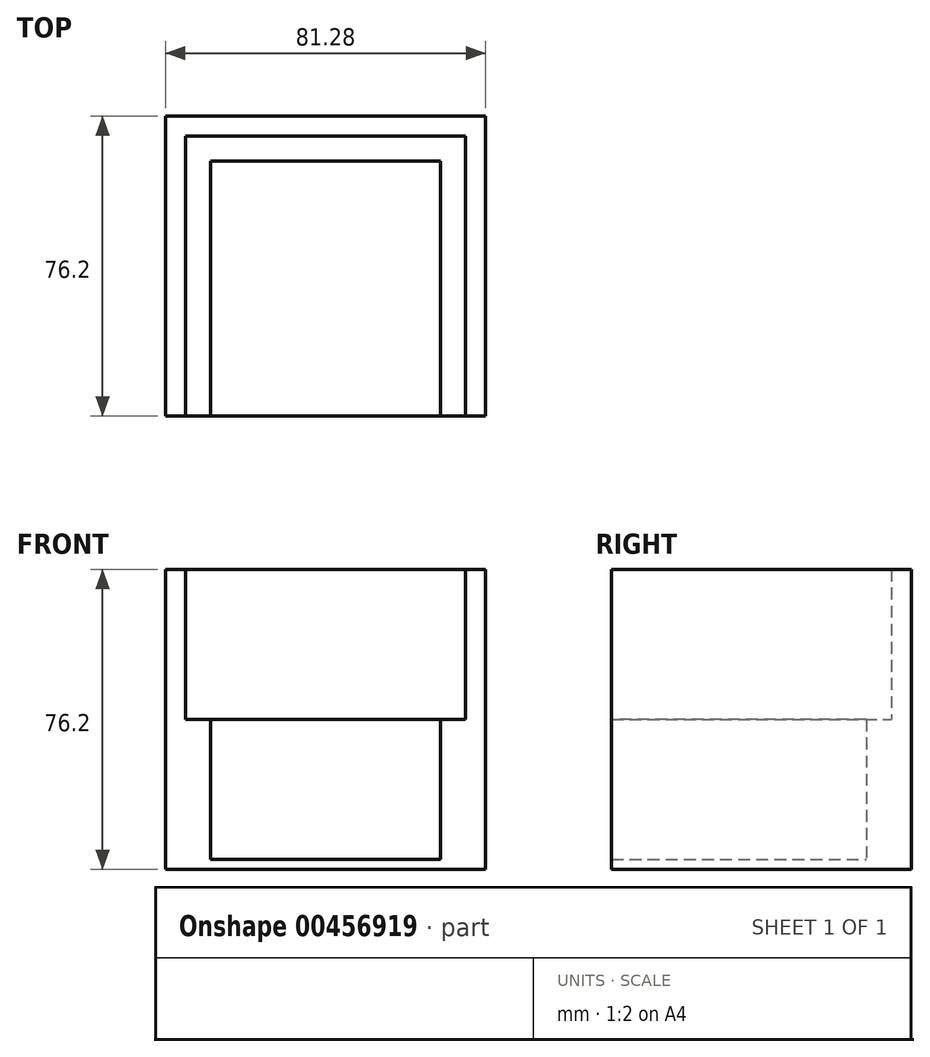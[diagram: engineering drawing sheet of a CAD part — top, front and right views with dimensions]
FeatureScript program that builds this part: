
annotation { "Feature Type Name" : "Feature", "Feature Type Description" : "" }
export const myFeature = defineFeature(function(context is Context, id is Id, definition is map)
    precondition{}
    {
        {
            var Q0;
            Q0=qCreatedBy(makeId("Top.planeOp"),FACE);
            var sketch = newSketch(context, id + "F0", { "sketchPlane" : qUnion([Q0])});
            skLineSegment(sketch, "E0", {"start": v(-27.81, -24.4) * mm, "end": v(-27.81, 51.8) * mm});
            skLineSegment(sketch, "E1", {"start": v(-27.81, 51.8) * mm, "end": v(53.47, 51.8) * mm});
            skLineSegment(sketch, "E2", {"start": v(53.47, 51.8) * mm, "end": v(53.47, -24.4) * mm});
            skLineSegment(sketch, "E3", {"start": v(53.47, -24.4) * mm, "end": v(48.39, -24.4) * mm});
            skLineSegment(sketch, "E4", {"start": v(48.39, -24.4) * mm, "end": v(48.39, 46.71) * mm});
            skLineSegment(sketch, "E5", {"start": v(48.39, 46.71) * mm, "end": v(-22.73, 46.71) * mm});
            skLineSegment(sketch, "E6", {"start": v(-22.73, 46.71) * mm, "end": v(-22.73, -24.4) * mm});
            skLineSegment(sketch, "E7", {"start": v(-22.73, -24.4) * mm, "end": v(-27.81, -24.4) * mm});
            skSolve(sketch);
        }
        {
            var Q0;
            Q0 = qSketchRegion(id + "F0", true);
            extrude(context, id + "F1", {"entities" : qUnion([Q0]), "depth" : 76.2 * mm});
        }
        {
            var Q0;
            Q0=qCreatedBy(makeId("Top.planeOp"),FACE);
            var sketch = newSketch(context, id + "F2", { "sketchPlane" : qUnion([Q0])});
            skLineSegment(sketch, "E8.bottom", {"start": v(-22.73, -24.4) * mm, "end": v(-16.38, -24.4) * mm});
            skLineSegment(sketch, "E8.top", {"start": v(-22.73, 46.71) * mm, "end": v(-16.38, 46.71) * mm});
            skLineSegment(sketch, "E8.left", {"start": v(-22.73, -24.4) * mm, "end": v(-22.73, 46.71) * mm});
            skLineSegment(sketch, "E9.bottom", {"start": v(48.39, -24.4) * mm, "end": v(42.04, -24.4) * mm});
            skLineSegment(sketch, "E9.top", {"start": v(48.39, 46.71) * mm, "end": v(42.04, 46.71) * mm});
            skLineSegment(sketch, "E9.left", {"start": v(48.39, -24.4) * mm, "end": v(48.39, 46.71) * mm});
            skLineSegment(sketch, "E10", {"start": v(-16.38, 46.71) * mm, "end": v(-16.38, -24.4) * mm});
            skLineSegment(sketch, "E11", {"start": v(42.04, 46.71) * mm, "end": v(42.04, -24.4) * mm});
            skSolve(sketch);
        }
        {
            var Q0;
            Q0 = qSketchRegion(id + "F2", true);
            extrude(context, id + "F3", {"entities" : qUnion([Q0]), "operationType" : NewBodyOperationType.ADD, "depth" : 38.1 * mm});
        }
        {
            var Q0;
            Q0=qCreatedBy(makeId("Top.planeOp"),FACE);
            var sketch = newSketch(context, id + "F4", { "sketchPlane" : qUnion([Q0])});
            skLineSegment(sketch, "E12.bottom", {"start": v(-16.38, -24.4) * mm, "end": v(42.04, -24.4) * mm});
            skLineSegment(sketch, "E12.top", {"start": v(-16.38, 46.71) * mm, "end": v(42.04, 46.71) * mm});
            skLineSegment(sketch, "E12.left", {"start": v(-16.38, -24.4) * mm, "end": v(-16.38, 46.71) * mm});
            skLineSegment(sketch, "E12.right", {"start": v(42.04, -24.4) * mm, "end": v(42.04, 46.71) * mm});
            skSolve(sketch);
        }
        {
            var Q0;
            Q0 = qSketchRegion(id + "F4", true);
            extrude(context, id + "F5", {"entities" : qUnion([Q0]), "operationType" : NewBodyOperationType.ADD, "depth" : 2.54 * mm});
        }
        {
            var Q0;
            Q0=qCreatedBy(makeId("Top.planeOp"),FACE);
            var sketch = newSketch(context, id + "F6", { "sketchPlane" : qUnion([Q0])});
            skLineSegment(sketch, "E13.bottom", {"start": v(-16.38, 46.71) * mm, "end": v(42.04, 46.71) * mm});
            skLineSegment(sketch, "E13.top", {"start": v(-16.38, 40.36) * mm, "end": v(42.04, 40.36) * mm});
            skLineSegment(sketch, "E13.left", {"start": v(-16.38, 46.71) * mm, "end": v(-16.38, 40.36) * mm});
            skLineSegment(sketch, "E13.right", {"start": v(42.04, 46.71) * mm, "end": v(42.04, 40.36) * mm});
            skSolve(sketch);
        }
        {
            var Q0;
            Q0 = qSketchRegion(id + "F6", true);
            extrude(context, id + "F7", {"entities" : qUnion([Q0]), "operationType" : NewBodyOperationType.ADD, "depth" : 38.1 * mm});
        }
    });
